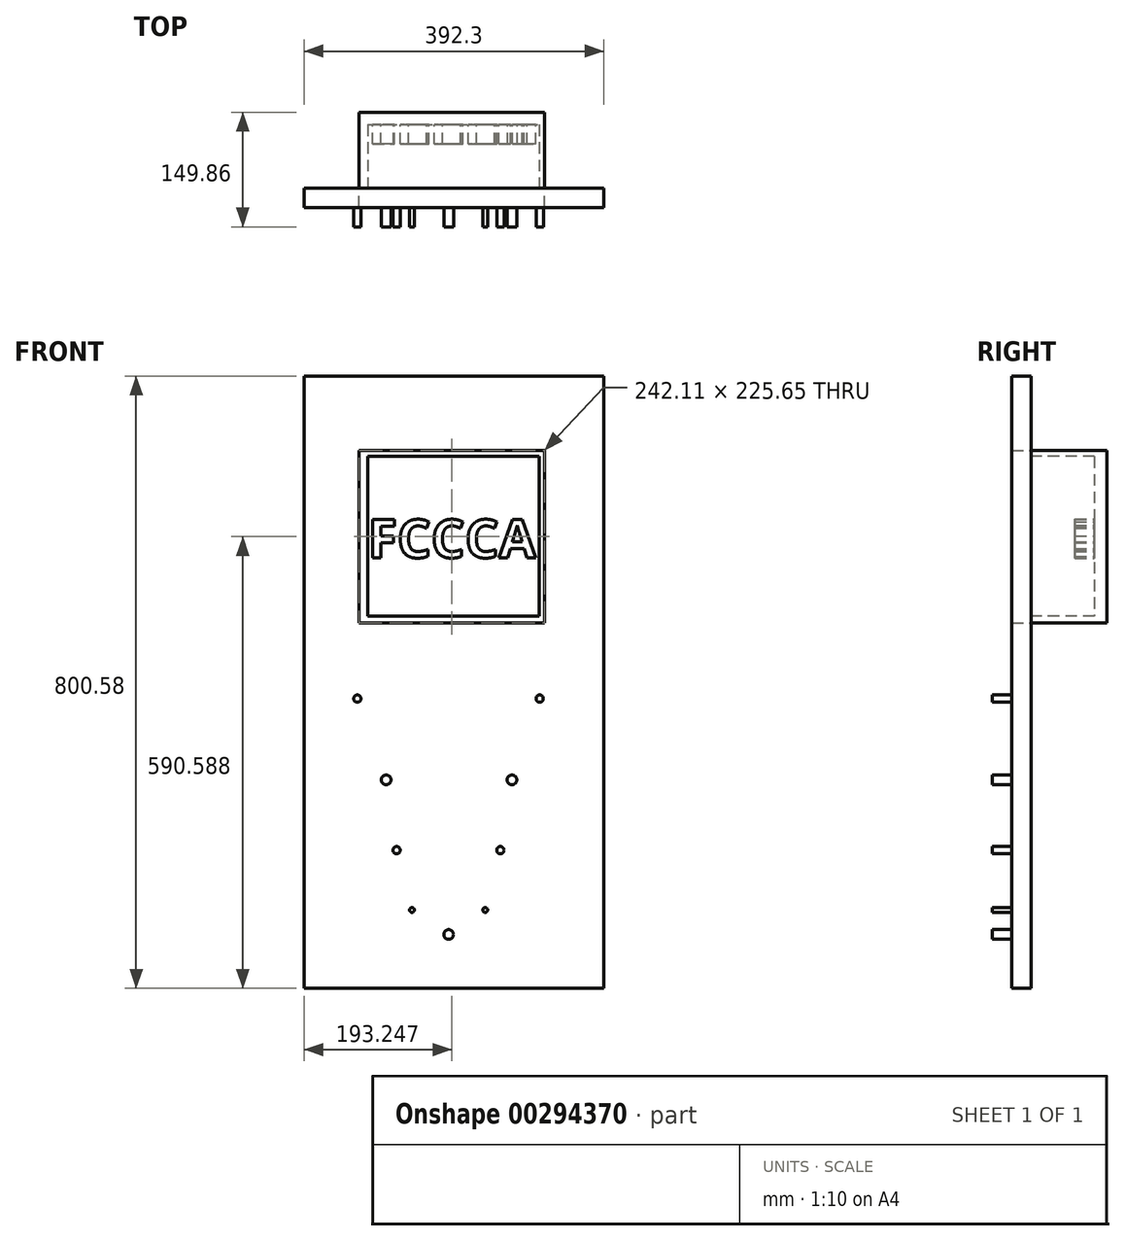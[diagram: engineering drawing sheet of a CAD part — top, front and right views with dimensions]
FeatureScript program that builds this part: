
annotation { "Feature Type Name" : "Feature", "Feature Type Description" : "" }
export const myFeature = defineFeature(function(context is Context, id is Id, definition is map)
    precondition{}
    {
        {
            var Q0;
            Q0=qCreatedBy(makeId("Front.planeOp"),FACE);
            var sketch = newSketch(context, id + "F0", { "sketchPlane" : qUnion([Q0])});
            skLineSegment(sketch, "E0.bottom", {"start": v(-189.19, 680.8) * mm, "end": v(203.11, 680.8) * mm});
            skLineSegment(sketch, "E0.top", {"start": v(-189.19, -119.77) * mm, "end": v(203.11, -119.77) * mm});
            skLineSegment(sketch, "E0.left", {"start": v(-189.19, 680.8) * mm, "end": v(-189.19, -119.77) * mm});
            skLineSegment(sketch, "E0.right", {"start": v(203.11, 680.8) * mm, "end": v(203.11, -119.77) * mm});
            skPoint(sketch, "E1.center.orphan", {"position": v(0, -46.27) * mm});
            skPoint(sketch, "E2.center.orphan", {"position": v(-34.4, 43.3) * mm});
            skPoint(sketch, "E3.center.orphan", {"position": v(-44.16, 6.14) * mm});
            skPoint(sketch, "E4.center.orphan", {"position": v(-28.6, -25.68) * mm});
            skPoint(sketch, "E5.center.orphan", {"position": v(33.88, -25.68) * mm});
            skPoint(sketch, "E6.center.orphan", {"position": v(48.05, 6.14) * mm});
            skPoint(sketch, "E7.center.orphan", {"position": v(40.62, 43.3) * mm});
            skLineSegment(sketch, "E8.bottom", {"start": v(-117, 583.64) * mm, "end": v(125.11, 583.64) * mm});
            skLineSegment(sketch, "E8.top", {"start": v(-117, 358) * mm, "end": v(125.11, 358) * mm});
            skLineSegment(sketch, "E8.left", {"start": v(-117, 583.64) * mm, "end": v(-117, 358) * mm});
            skLineSegment(sketch, "E8.right", {"start": v(125.11, 583.64) * mm, "end": v(125.11, 358) * mm});
            skSolve(sketch);
        }
        {
            var Q0;
            Q0=makeQuery(id+"F0.imprint","IMPRINT",FACE,{"disambiguationData":[TD([[makeQuery(id+"F0.imprint","IMPRINT",EDGE,{"derivedFrom":sQuery(id+"F0.wireOp",EDGE,"E0.bottom")}),-1.0]])]});
            extrude(context, id + "F1", {"entities" : qUnion([Q0]), "depth" : 25.4 * mm});
        }
        {
            var Q0;
            Q0=makeQuery(id+"F1.opExtrude","CAP_FACE",FACE,{"disambiguationData":[OSD([sQuery(id+"F0.wireOp",EDGE,"E0.bottom"),sQuery(id+"F0.wireOp",EDGE,"E0.top"),sQuery(id+"F0.wireOp",EDGE,"E0.left"),sQuery(id+"F0.wireOp",EDGE,"E0.right")])],"isStart":false});
            var sketch = newSketch(context, id + "F2", { "sketchPlane" : qUnion([Q0])});
            skCircle(sketch, "E9", {"center": v(0, -49.3) * mm, "radius": 6.35 * mm});
            skCircle(sketch, "E10", {"center": v(-47.89, -17.26) * mm, "radius": 3.18 * mm});
            skCircle(sketch, "E11", {"center": v(-68.06, 60.9) * mm, "radius": 4.76 * mm});
            skCircle(sketch, "E12", {"center": v(-81.76, 152.83) * mm, "radius": 6.35 * mm});
            skCircle(sketch, "E13", {"center": v(47.87, -17.26) * mm, "radius": 3.18 * mm});
            skCircle(sketch, "E14", {"center": v(67.62, 60.9) * mm, "radius": 4.76 * mm});
            skCircle(sketch, "E15", {"center": v(82.8, 152.83) * mm, "radius": 6.35 * mm});
            skCircle(sketch, "E16", {"center": v(-119.37, 259.1) * mm, "radius": 4.76 * mm});
            skCircle(sketch, "E17", {"center": v(119.08, 259.1) * mm, "radius": 4.76 * mm});
            skSolve(sketch);
        }
        {
            var Q0;
            Q0 = qSketchRegion(id + "F2", true);
            extrude(context, id + "F3", {"entities" : qUnion([Q0]), "operationType" : NewBodyOperationType.ADD, "depth" : 25.4 * mm});
        }
        {
            var Q0;
            Q0=makeQuery(id+"F1.opExtrude","CAP_FACE",FACE,{"disambiguationData":[OSD([sQuery(id+"F0.wireOp",EDGE,"E0.bottom"),sQuery(id+"F0.wireOp",EDGE,"E0.top"),sQuery(id+"F0.wireOp",EDGE,"E0.left"),sQuery(id+"F0.wireOp",EDGE,"E0.right"),sQuery(id+"F0.wireOp",EDGE,"E8.bottom"),sQuery(id+"F0.wireOp",EDGE,"E8.top"),sQuery(id+"F0.wireOp",EDGE,"E8.left"),sQuery(id+"F0.wireOp",EDGE,"E8.right")])],"isStart":true});
            var sketch = newSketch(context, id + "F4", { "sketchPlane" : qUnion([Q0])});
            skLineSegment(sketch, "E18.bottom", {"start": v(-125.11, 358) * mm, "end": v(117, 358) * mm});
            skLineSegment(sketch, "E18.top", {"start": v(-125.11, 583.64) * mm, "end": v(117, 583.64) * mm});
            skLineSegment(sketch, "E18.left", {"start": v(-125.11, 358) * mm, "end": v(-125.11, 583.64) * mm});
            skLineSegment(sketch, "E18.right", {"start": v(117, 358) * mm, "end": v(117, 583.64) * mm});
            skSolve(sketch);
        }
        {
            var Q0;
            Q0 = qSketchRegion(id + "F4", true);
            extrude(context, id + "F5", {"entities" : qUnion([Q0]), "depth" : 99.06 * mm});
        }
        {
            var Q0;
            Q0=makeQuery(id+"F5.opExtrude","CAP_FACE",FACE,{"disambiguationData":[OSD([sQuery(id+"F4.wireOp",EDGE,"E18.bottom"),sQuery(id+"F4.wireOp",EDGE,"E18.top"),sQuery(id+"F4.wireOp",EDGE,"E18.left"),sQuery(id+"F4.wireOp",EDGE,"E18.right")])],"isStart":true});
            var sketch = newSketch(context, id + "F6", { "sketchPlane" : qUnion([Q0])});
            skLineSegment(sketch, "E19.bottom", {"start": v(-105.48, 575.54) * mm, "end": v(118.2, 575.54) * mm});
            skLineSegment(sketch, "E19.top", {"start": v(-105.48, 366.6) * mm, "end": v(118.2, 366.6) * mm});
            skLineSegment(sketch, "E19.left", {"start": v(-105.48, 575.54) * mm, "end": v(-105.48, 366.6) * mm});
            skLineSegment(sketch, "E19.right", {"start": v(118.2, 575.54) * mm, "end": v(118.2, 366.6) * mm});
            skSolve(sketch);
        }
        {
            var Q0;
            Q0=makeQuery(id+"F6.imprint","IMPRINT",FACE,{"disambiguationData":[TD([[makeQuery(id+"F6.imprint","IMPRINT",EDGE,{"derivedFrom":sQuery(id+"F6.wireOp",EDGE,"E19.bottom")}),-1.0]])]});
            extrude(context, id + "F7", {"entities" : qUnion([Q0]), "operationType" : NewBodyOperationType.REMOVE, "oppositeDirection" : true, "depth" : 82.8 * mm});
        }
        {
            var Q0;
            Q0=makeQuery(id+"F7.boolean.opBoolean","COPY",FACE,{"derivedFrom":makeQuery(id+"F7.opExtrude","CAP_FACE",FACE,{"disambiguationData":[OSD([sQuery(id+"F6.wireOp",EDGE,"E19.bottom"),sQuery(id+"F6.wireOp",EDGE,"E19.top"),sQuery(id+"F6.wireOp",EDGE,"E19.left"),sQuery(id+"F6.wireOp",EDGE,"E19.right")])],"isStart":false})});
            var sketch = newSketch(context, id + "F8", { "sketchPlane" : qUnion([Q0])});
            skText(sketch, "E20", { "text": "FCCCA", "fontName": "OpenSans-Bold.ttf"});
            const initialGuessF8  = {"E20": [-0.10548, 0.44327, 1, 0, 0.05009]};
            skSetInitialGuess(sketch, initialGuessF8);
            skSolve(sketch);
        }
        {
            var Q0;
            Q0 = qSketchRegion(id + "F8", true);
            extrude(context, id + "F9", {"entities" : qUnion([Q0]), "operationType" : NewBodyOperationType.ADD, "depth" : 25.4 * mm});
        }
    });
